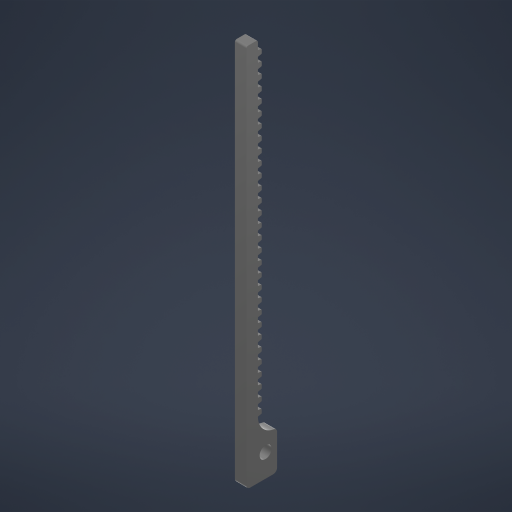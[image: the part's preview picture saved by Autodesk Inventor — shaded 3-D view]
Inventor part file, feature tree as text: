
AUTODESK INVENTOR PART (.ipt)
format: ipt  version: 2023 (Build 270158000, 158)  size: 564,736 bytes
history: native  units: mm
features: extrude x2, sketch x2, fillet x1
ambient origin geometry x8: Origin, YZ Plane, XZ Plane, XY Plane, X Axis, Y Axis, Z Axis, Center Point
bodies: Solid1 (feature_tree)
feature tree (5):
  extrude  "Extrusion1"  Depth=8.0mm
  fillet  "Fillet1"  Radius=90.0mm
  extrude  "Extrusion2"  Depth=3.0mm TaperAngle=0.0deg
  sketch  "Sketch1"  dims[d0=10.0mm d1=8.0mm d2=90.0mm]
  sketch  "Sketch3"  dims[d3=3.0mm d4=3.0mm d5=0.0mm d6=3.1mm d7=5.0mm d8=4.0mm d9=5.0mm d10=1.0mm d11=0.5mm d12=1.0mm d13=0.75mm d14=0.2mm d15=0.1mm d16=0.1mm d17=300.0mm d19=2.8mm d20=10.0mm d22=10.0mm d24=10.0mm d25=0.0mm]
